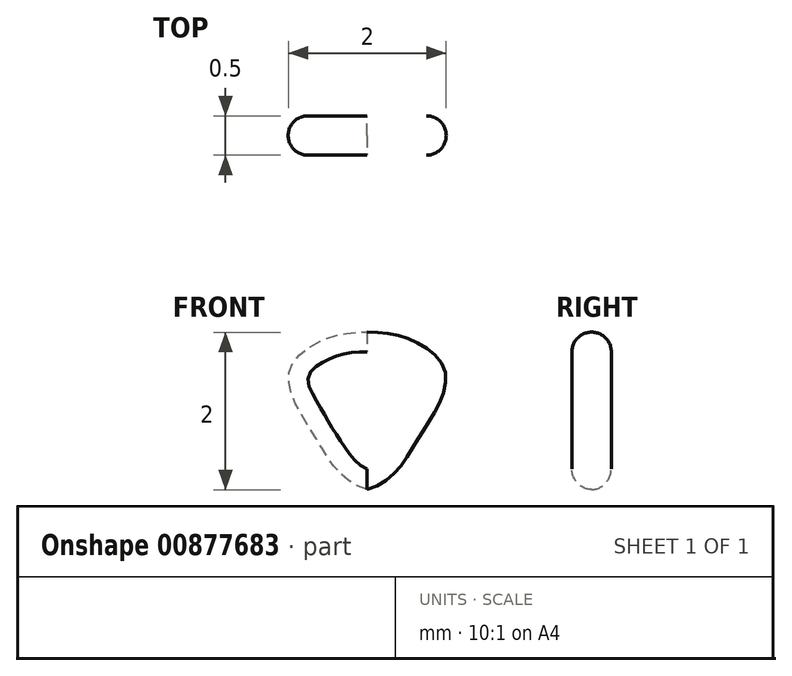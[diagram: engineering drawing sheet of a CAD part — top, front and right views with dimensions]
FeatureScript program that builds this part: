
annotation { "Feature Type Name" : "Feature", "Feature Type Description" : "" }
export const myFeature = defineFeature(function(context is Context, id is Id, definition is map)
    precondition{}
    {
        {
            var Q0;
            Q0=qCreatedBy(makeId("Front.planeOp"),FACE);
            var sketch = newSketch(context, id + "F0", { "sketchPlane" : qUnion([Q0])});
            skFitSpline(sketch, "E0", {"points": [v(0, 4.14) * mm, v(0.45, 4.08) * mm, v(0.87, 3.84) * mm, v(1, 3.53) * mm, v(0.86, 3.15) * mm, v(0.5, 2.54) * mm, v(0.2, 2.22) * mm, v(0, 2.14) * mm], "startDerivative": vector(3.32, 0.11) * mm, "endDerivative": vector(-1.97, -0.56) * mm});
            skLineSegment(sketch, "E1", {"start": v(0, 4.14) * mm, "end": v(0, 2.14) * mm});
            skFitSpline(sketch, "E2.MirrorCS", {"points": [v(0, 4.14) * mm, v(-0.45, 4.08) * mm, v(-0.87, 3.84) * mm, v(-1, 3.53) * mm, v(-0.86, 3.15) * mm, v(-0.5, 2.54) * mm, v(-0.2, 2.22) * mm, v(0, 2.14) * mm], "startDerivative": vector(-3.32, 0.11) * mm, "endDerivative": vector(1.97, -0.56) * mm});
            skSolve(sketch);
        }
        {
            var Q0;
            Q0=makeQuery(id+"F0.imprint","IMPRINT",FACE,{"disambiguationData":[TD([[makeQuery(id+"F0.imprint","IMPRINT",EDGE,{"derivedFrom":sQuery(id+"F0.wireOp",EDGE,"E0")}),-1.0]])]});
            var Q1;
            Q1=makeQuery(id+"F0.imprint","IMPRINT",FACE,{"disambiguationData":[TD([[makeQuery(id+"F0.imprint","IMPRINT",EDGE,{"derivedFrom":sQuery(id+"F0.wireOp",EDGE,"E1")}),-1.0]])]});
            extrude(context, id + "F1", {"entities" : qUnion([Q0, Q1]), "depth" : .5 * mm, "offsetDistance" : 25 * mm});
        }
        {
            var Q0;
            Q0=makeQuery(id+"F1.opExtrude","CAP_EDGE",EDGE,{"disambiguationData":[OSD([sQuery(id+"F0.wireOp",EDGE,"E2.MirrorCS")])],"isStart":false});
            var Q1;
            Q1=makeQuery(id+"F1.opExtrude","CAP_EDGE",EDGE,{"disambiguationData":[OSD([sQuery(id+"F0.wireOp",EDGE,"E2.MirrorCS")])],"isStart":true});
            var Q2;
            Q2=makeQuery(id+"F1.opExtrude","CAP_EDGE",EDGE,{"disambiguationData":[OSD([sQuery(id+"F0.wireOp",EDGE,"E0")])],"isStart":false});
            var Q3;
            Q3=makeQuery(id+"F1.opExtrude","CAP_EDGE",EDGE,{"disambiguationData":[OSD([sQuery(id+"F0.wireOp",EDGE,"E0")])],"isStart":true});
            fillet(context, id + "F2", {"entities" : qUnion([Q0, Q1, Q2, Q3]), "radius" : .25 * mm, "tangentPropagation" : true, "allowEdgeOverflow" : false});
        }
    });
